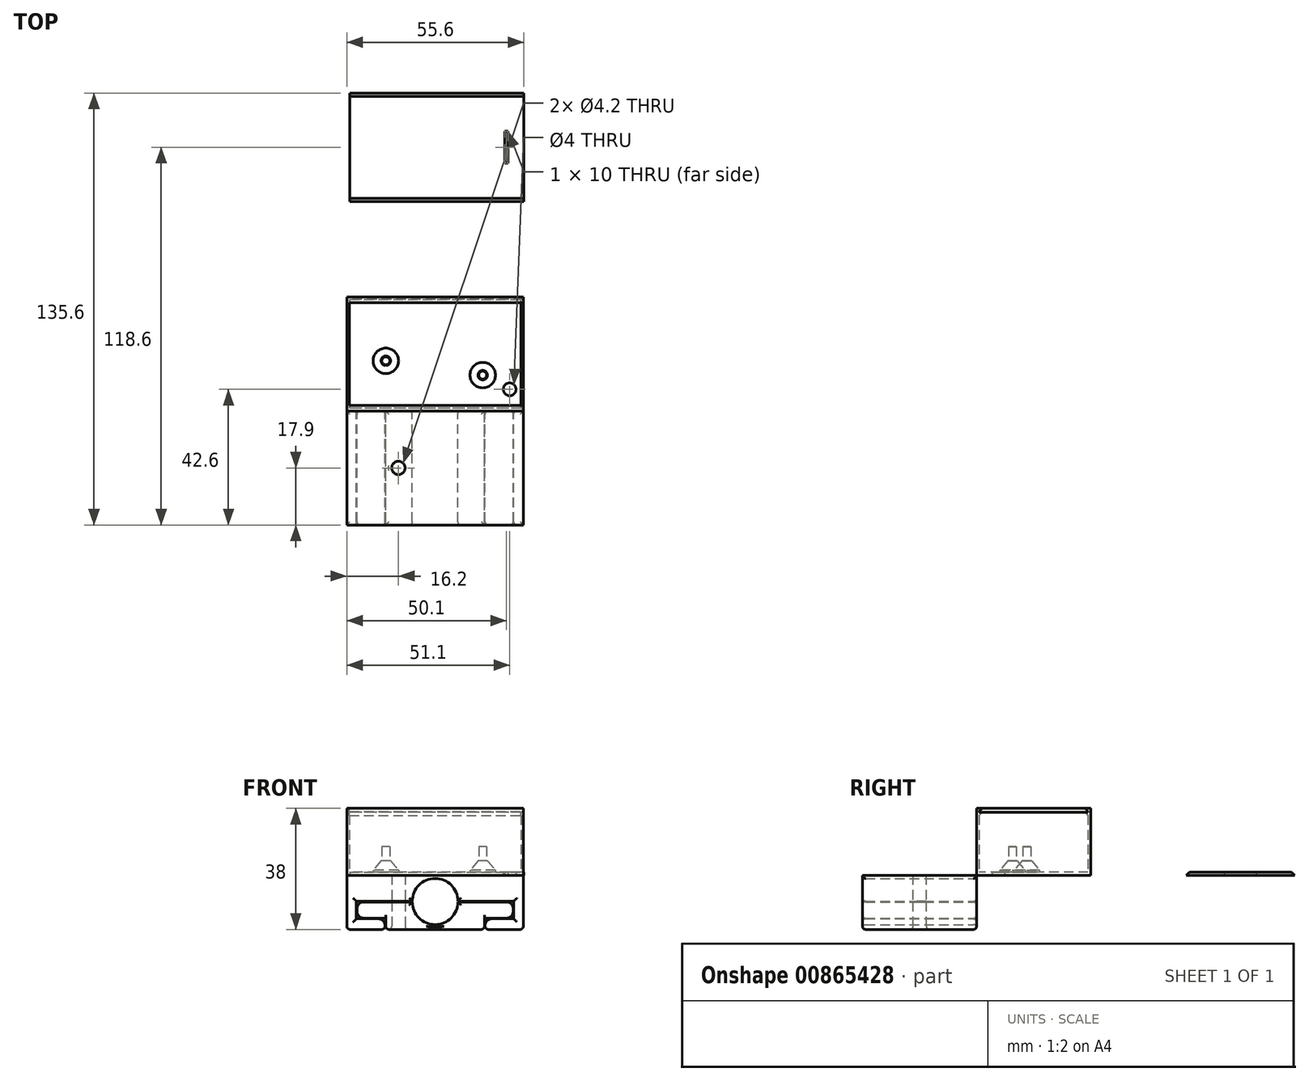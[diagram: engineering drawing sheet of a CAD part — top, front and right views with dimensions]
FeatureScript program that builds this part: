
annotation { "Feature Type Name" : "Feature", "Feature Type Description" : "" }
export const myFeature = defineFeature(function(context is Context, id is Id, definition is map)
    precondition{}
    {
        {
            var Q0;
            Q0=qCreatedBy(makeId("Top.planeOp"),FACE);
            var sketch = newSketch(context, id + "F0", { "sketchPlane" : qUnion([Q0])});
            skLineSegment(sketch, "E0.bottom", {"start": v(0, 0) * mm, "end": v(53.8, 0) * mm});
            skLineSegment(sketch, "E0.top", {"start": v(0, -34.2) * mm, "end": v(53.8, -34.2) * mm});
            skLineSegment(sketch, "E0.left", {"start": v(0, 0) * mm, "end": v(0, -34.2) * mm});
            skLineSegment(sketch, "E0.right", {"start": v(53.8, 0) * mm, "end": v(53.8, -34.2) * mm});
            skLineSegment(sketch, "E1.0", {"start": v(-0.8, 0.8) * mm, "end": v(54.6, 0.8) * mm});
            skLineSegment(sketch, "E1.1", {"start": v(-0.8, 0.8) * mm, "end": v(-0.8, -35) * mm});
            skLineSegment(sketch, "E1.2", {"start": v(-0.8, -35) * mm, "end": v(54.6, -35) * mm});
            skLineSegment(sketch, "E1.3", {"start": v(54.6, 0.8) * mm, "end": v(54.6, -35) * mm});
            skCircle(sketch, "E2", {"center": v(11.45, -19.25) * mm, "radius": 1.25 * mm});
            skCircle(sketch, "E3", {"center": v(11.45, -19.25) * mm, "radius": 4 * mm});
            skCircle(sketch, "E4", {"center": v(41.85, -23.75) * mm, "radius": 1.25 * mm});
            skCircle(sketch, "E5", {"center": v(41.85, -23.75) * mm, "radius": 4 * mm});
            skCircle(sketch, "E6", {"center": v(50.3, -28.2) * mm, "radius": 2 * mm});
            skLineSegment(sketch, "E7.bottom", {"start": v(54.8, 30.8) * mm, "end": v(0.2, 30.8) * mm});
            skLineSegment(sketch, "E7.top", {"start": v(54.8, 64.8) * mm, "end": v(0.2, 64.8) * mm});
            skLineSegment(sketch, "E7.left", {"start": v(54.8, 30.8) * mm, "end": v(54.8, 64.8) * mm});
            skLineSegment(sketch, "E7.right", {"start": v(0.2, 30.8) * mm, "end": v(0.2, 64.8) * mm});
            skLineSegment(sketch, "E8.bottom", {"start": v(48.8, 42.8) * mm, "end": v(49.8, 42.8) * mm});
            skLineSegment(sketch, "E8.top", {"start": v(48.8, 52.8) * mm, "end": v(49.8, 52.8) * mm});
            skLineSegment(sketch, "E8.left", {"start": v(48.8, 42.8) * mm, "end": v(48.8, 52.8) * mm});
            skLineSegment(sketch, "E8.right", {"start": v(49.8, 42.8) * mm, "end": v(49.8, 52.8) * mm});
            skLineSegment(sketch, "E9", {"start": v(54.8, 47.8) * mm, "end": v(0.2, 47.8) * mm, "construction": true});
            skLineSegment(sketch, "E10", {"start": v(49.8, 47.8) * mm, "end": v(48.8, 47.8) * mm, "construction": true});
            skSolve(sketch);
        }
        {
            var Q0;
            Q0=makeQuery(id+"F0.imprint","IMPRINT",FACE,{"disambiguationData":[TD([[makeQuery(id+"F0.imprint","IMPRINT",EDGE,{"derivedFrom":sQuery(id+"F0.wireOp",EDGE,"E0.bottom")}),1.0]])]});
            extrude(context, id + "F1", {"entities" : qUnion([Q0]), "depth" : 21 * mm, "offsetDistance" : 25 * mm});
        }
        {
            var Q0;
            Q0=makeQuery(id+"F0.imprint","IMPRINT",FACE,{"disambiguationData":[TD([[makeQuery(id+"F0.imprint","IMPRINT",EDGE,{"derivedFrom":sQuery(id+"F0.wireOp",EDGE,"E0.bottom")}),-1.0]])]});
            var Q1;
            Q1=makeQuery(id+"F0.imprint","IMPRINT",FACE,{"disambiguationData":[TD([[makeQuery(id+"F0.imprint","IMPRINT",EDGE,{"derivedFrom":sQuery(id+"F0.wireOp",EDGE,"E2")}),-1.0]])]});
            var Q2;
            Q2=makeQuery(id+"F0.imprint","IMPRINT",FACE,{"disambiguationData":[TD([[makeQuery(id+"F0.imprint","IMPRINT",EDGE,{"derivedFrom":sQuery(id+"F0.wireOp",EDGE,"E2")}),1.0]])]});
            var Q3;
            Q3=makeQuery(id+"F0.imprint","IMPRINT",FACE,{"disambiguationData":[TD([[makeQuery(id+"F0.imprint","IMPRINT",EDGE,{"derivedFrom":sQuery(id+"F0.wireOp",EDGE,"E4")}),-1.0]])]});
            var Q4;
            Q4=makeQuery(id+"F0.imprint","IMPRINT",FACE,{"disambiguationData":[TD([[makeQuery(id+"F0.imprint","IMPRINT",EDGE,{"derivedFrom":sQuery(id+"F0.wireOp",EDGE,"E4")}),1.0]])]});
            extrude(context, id + "F2", {"entities" : qUnion([Q0, Q1, Q2, Q3, Q4]), "operationType" : NewBodyOperationType.ADD, "depth" : 1 * mm, "offsetDistance" : 25 * mm});
        }
        {
            var Q0;
            Q0=makeQuery(id+"F0.imprint","IMPRINT",FACE,{"disambiguationData":[TD([[makeQuery(id+"F0.imprint","IMPRINT",EDGE,{"derivedFrom":sQuery(id+"F0.wireOp",EDGE,"E2")}),-1.0]])]});
            var Q1;
            Q1=makeQuery(id+"F0.imprint","IMPRINT",FACE,{"disambiguationData":[TD([[makeQuery(id+"F0.imprint","IMPRINT",EDGE,{"derivedFrom":sQuery(id+"F0.wireOp",EDGE,"E2")}),1.0]])]});
            var Q2;
            Q2=makeQuery(id+"F0.imprint","IMPRINT",FACE,{"disambiguationData":[TD([[makeQuery(id+"F0.imprint","IMPRINT",EDGE,{"derivedFrom":sQuery(id+"F0.wireOp",EDGE,"E4")}),1.0]])]});
            var Q3;
            Q3=makeQuery(id+"F0.imprint","IMPRINT",FACE,{"disambiguationData":[TD([[makeQuery(id+"F0.imprint","IMPRINT",EDGE,{"derivedFrom":sQuery(id+"F0.wireOp",EDGE,"E4")}),-1.0]])]});
            extrude(context, id + "F3", {"entities" : qUnion([Q0, Q1, Q2, Q3]), "operationType" : NewBodyOperationType.ADD, "depth" : 4.6 * mm, "offsetDistance" : 25 * mm});
        }
        {
            var Q0;
            Q0=makeQuery(id+"F0.imprint","IMPRINT",FACE,{"disambiguationData":[TD([[makeQuery(id+"F0.imprint","IMPRINT",EDGE,{"derivedFrom":sQuery(id+"F0.wireOp",EDGE,"E4")}),1.0]])]});
            var Q1;
            Q1=makeQuery(id+"F0.imprint","IMPRINT",FACE,{"disambiguationData":[TD([[makeQuery(id+"F0.imprint","IMPRINT",EDGE,{"derivedFrom":sQuery(id+"F0.wireOp",EDGE,"E2")}),1.0]])]});
            extrude(context, id + "F4", {"entities" : qUnion([Q0, Q1]), "operationType" : NewBodyOperationType.ADD, "depth" : 9 * mm, "offsetDistance" : 25 * mm});
        }
        {
            var Q0;
            Q0=makeQuery(id+"F3.opExtrude","CAP_EDGE",EDGE,{"disambiguationData":[OSD([sQuery(id+"F0.wireOp",EDGE,"E5")])],"isStart":false});
            var Q1;
            Q1=makeQuery(id+"F3.opExtrude","CAP_EDGE",EDGE,{"disambiguationData":[OSD([sQuery(id+"F0.wireOp",EDGE,"E3")])],"isStart":false});
            chamfer(context, id + "F5", {"entities" : qUnion([Q0, Q1]), "chamferType" : ChamferType.TWO_OFFSETS, "width1" : 2.5 * mm, "oppositeDirection" : false, "width2" : 3 * mm, "tangentPropagation" : true});
        }
        {
            var Q0;
            Q0=makeQuery(id+"F1.opExtrude","SWEPT_FACE",FACE,{"disambiguationData":[OSD([sQuery(id+"F0.wireOp",EDGE,"E0.top")])]});
            var sketch = newSketch(context, id + "F6", { "sketchPlane" : qUnion([Q0])});
            skLineSegment(sketch, "E11", {"start": v(-53.8, 20) * mm, "end": v(0, 20) * mm});
            skLineSegment(sketch, "E12", {"start": v(-53.8, 19.8) * mm, "end": v(0, 19.8) * mm});
            skLineSegment(sketch, "E13", {"start": v(-53.8, 18.8) * mm, "end": v(0, 18.8) * mm});
            skSolve(sketch);
        }
        {
            var Q0;
            Q0=makeQuery(id+"F1.opExtrude","SWEPT_FACE",FACE,{"disambiguationData":[OSD([sQuery(id+"F0.wireOp",EDGE,"E0.bottom")])]});
            var sketch = newSketch(context, id + "F7", { "sketchPlane" : qUnion([Q0])});
            skLineSegment(sketch, "E14", {"start": v(0, 20) * mm, "end": v(53.8, 20) * mm});
            skLineSegment(sketch, "E15", {"start": v(53.8, 19.8) * mm, "end": v(0, 19.8) * mm});
            skLineSegment(sketch, "E16", {"start": v(0, 18.8) * mm, "end": v(53.8, 18.8) * mm});
            skSolve(sketch);
        }
        {
            var Q0;
            {var subQ0=sQuery(id+"F6.wireOp",EDGE,"E11");Q0=makeQuery(id+"F6.imprint","IMPRINT",FACE,{"disambiguationData":[TD([[makeQuery(id+"F6.imprint","IMPRINT",EDGE,{"derivedFrom":subQ0}),1.0]])]});}
            var Q1;
            {var subQ0=sQuery(id+"F6.wireOp",EDGE,"E12");Q1=makeQuery(id+"F6.imprint","IMPRINT",FACE,{"disambiguationData":[TD([[makeQuery(id+"F6.imprint","IMPRINT",EDGE,{"derivedFrom":subQ0}),-1.0]])]});}
            extrude(context, id + "F8", {"entities" : qUnion([Q0, Q1]), "operationType" : NewBodyOperationType.ADD, "depth" : 1 * mm, "offsetDistance" : 25 * mm});
        }
        {
            var Q0;
            {var subQ0=sQuery(id+"F7.wireOp",EDGE,"E15");Q0=makeQuery(id+"F7.imprint","IMPRINT",FACE,{"disambiguationData":[TD([[makeQuery(id+"F7.imprint","IMPRINT",EDGE,{"derivedFrom":subQ0}),1.0]])]});}
            var Q1;
            {var subQ0=sQuery(id+"F7.wireOp",EDGE,"E14");Q1=makeQuery(id+"F7.imprint","IMPRINT",FACE,{"disambiguationData":[TD([[makeQuery(id+"F7.imprint","IMPRINT",EDGE,{"derivedFrom":subQ0}),1.0]])]});}
            extrude(context, id + "F9", {"entities" : qUnion([Q0, Q1]), "operationType" : NewBodyOperationType.ADD, "depth" : 1 * mm, "offsetDistance" : 25 * mm});
        }
        {
            var Q0;
            Q0=makeQuery(id+"F9.opExtrude","CAP_EDGE",EDGE,{"disambiguationData":[OSD([sQuery(id+"F7.wireOp",EDGE,"E16")])],"isStart":false});
            var Q1;
            Q1=makeQuery(id+"F9.opExtrude","CAP_EDGE",EDGE,{"disambiguationData":[OSD([sQuery(id+"F7.wireOp",EDGE,"E14")])],"isStart":false});
            var Q2;
            Q2=makeQuery(id+"F8.opExtrude","CAP_EDGE",EDGE,{"disambiguationData":[OSD([sQuery(id+"F6.wireOp",EDGE,"E13")])],"isStart":false});
            var Q3;
            Q3=makeQuery(id+"F8.opExtrude","CAP_EDGE",EDGE,{"disambiguationData":[OSD([sQuery(id+"F6.wireOp",EDGE,"E11")])],"isStart":false});
            chamfer(context, id + "F10", {"entities" : qUnion([Q0, Q1, Q2, Q3]), "width" : 1 * mm, "tangentPropagation" : true});
        }
        {
            var Q0;
            Q0=makeQuery(id+"F1.opExtrude","SWEPT_FACE",FACE,{"disambiguationData":[OSD([sQuery(id+"F0.wireOp",EDGE,"E0.right")])]});
            var sketch = newSketch(context, id + "F11", { "sketchPlane" : qUnion([Q0])});
            skLineSegment(sketch, "E17", {"start": v(1, 19.8) * mm, "end": v(33.2, 19.8) * mm});
            skSolve(sketch);
        }
        {
            var Q0;
            Q0=makeQuery(id+"F11.imprint","IMPRINT",FACE,{"disambiguationData":[TD([[makeQuery(id+"F11.imprint","IMPRINT",EDGE,{"derivedFrom":sQuery(id+"F11.wireOp",EDGE,"E17")}),1.0]])]});
            extrude(context, id + "F12", {"entities" : qUnion([Q0]), "operationType" : NewBodyOperationType.REMOVE, "endBound" : BoundingType.UP_TO_NEXT, "oppositeDirection" : true, "depth" : 25 * mm, "offsetDistance" : 25 * mm});
        }
        {
            var Q0;
            Q0=makeQuery(id+"F0.imprint","IMPRINT",FACE,{"disambiguationData":[TD([[makeQuery(id+"F0.imprint","IMPRINT",EDGE,{"derivedFrom":sQuery(id+"F0.wireOp",EDGE,"E7.bottom")}),-1.0]])]});
            extrude(context, id + "F13", {"entities" : qUnion([Q0]), "depth" : 1 * mm, "offsetDistance" : 25 * mm});
        }
        {
            var Q0;
            Q0=makeQuery(id+"F13.opExtrude","CAP_EDGE",EDGE,{"disambiguationData":[OSD([sQuery(id+"F0.wireOp",EDGE,"E7.bottom")])],"isStart":false});
            var Q1;
            Q1=makeQuery(id+"F13.opExtrude","CAP_EDGE",EDGE,{"disambiguationData":[OSD([sQuery(id+"F0.wireOp",EDGE,"E7.top")])],"isStart":false});
            chamfer(context, id + "F14", {"entities" : qUnion([Q0, Q1]), "width" : 1 * mm, "tangentPropagation" : true});
        }
        {
            var Q0;
            Q0=makeQuery(id+"F1.opExtrude","SWEPT_FACE",FACE,{"disambiguationData":[OSD([sQuery(id+"F0.wireOp",EDGE,"E1.2")])]});
            var sketch = newSketch(context, id + "F15", { "sketchPlane" : qUnion([Q0])});
            skLineSegment(sketch, "E18", {"start": v(26.9, -1) * mm, "end": v(26.9, -8.15) * mm, "construction": true});
            skArc(sketch, "E19", {"start": v(34.05, -8.15) * mm, "mid": v(26.9, -1) * mm, "end": v(19.75, -8.15) * mm});
            skLineSegment(sketch, "E20", {"start": v(54.6, 0) * mm, "end": v(54.6, -8.15) * mm});
            skLineSegment(sketch, "E21", {"start": v(-0.8, 0) * mm, "end": v(54.6, 0) * mm});
            skLineSegment(sketch, "E22", {"start": v(26.9, 0) * mm, "end": v(26.9, -1) * mm, "construction": true});
            skLineSegment(sketch, "E23", {"start": v(51.6, -8.15) * mm, "end": v(34.05, -8.15) * mm});
            skLineSegment(sketch, "E24", {"start": v(19.75, -8.15) * mm, "end": v(2.2, -8.15) * mm});
            skLineSegment(sketch, "E25", {"start": v(26.9, -8.15) * mm, "end": v(26.9, -15.5) * mm, "construction": true});
            skArc(sketch, "E26", {"start": v(19.75, -8.35) * mm, "mid": v(21.84, -13.4) * mm, "end": v(26.9, -15.5) * mm});
            skLineSegment(sketch, "E27", {"start": v(26.9, -17) * mm, "end": v(11.4, -17) * mm});
            skLineSegment(sketch, "E28", {"start": v(-0.8, 0) * mm, "end": v(-0.8, -17) * mm});
            skLineSegment(sketch, "E29", {"start": v(-0.8, -17) * mm, "end": v(11.2, -17) * mm});
            skLineSegment(sketch, "E30", {"start": v(11.2, -17) * mm, "end": v(11.2, -13.68) * mm});
            skLineSegment(sketch, "E31", {"start": v(11.2, -13.68) * mm, "end": v(2.2, -13.68) * mm});
            skLineSegment(sketch, "E32", {"start": v(2.2, -13.68) * mm, "end": v(2.2, -8.15) * mm});
            skLineSegment(sketch, "E33.1", {"start": v(19.75, -8.35) * mm, "end": v(2.4, -8.35) * mm});
            skLineSegment(sketch, "E33.2", {"start": v(2.4, -13.48) * mm, "end": v(2.4, -8.35) * mm});
            skLineSegment(sketch, "E33.3", {"start": v(11.4, -13.48) * mm, "end": v(2.4, -13.48) * mm});
            skLineSegment(sketch, "E34.MirrorCS", {"start": v(26.9, -17) * mm, "end": v(42.4, -17) * mm});
            skLineSegment(sketch, "E35.MirrorCS", {"start": v(42.4, -13.48) * mm, "end": v(51.4, -13.48) * mm});
            skLineSegment(sketch, "E36.MirrorCS", {"start": v(51.4, -13.48) * mm, "end": v(51.4, -8.35) * mm});
            skLineSegment(sketch, "E37.MirrorCS", {"start": v(34.05, -8.35) * mm, "end": v(51.4, -8.35) * mm});
            skArc(sketch, "E38.MirrorCS", {"start": v(34.05, -8.35) * mm, "mid": v(31.96, -13.4) * mm, "end": v(26.9, -15.5) * mm});
            skLineSegment(sketch, "E39.MirrorCS", {"start": v(42.6, -17) * mm, "end": v(42.6, -13.68) * mm});
            skLineSegment(sketch, "E40.MirrorCS", {"start": v(54.6, -17) * mm, "end": v(42.6, -17) * mm});
            skLineSegment(sketch, "E41.MirrorCS", {"start": v(42.6, -13.68) * mm, "end": v(51.6, -13.68) * mm});
            skLineSegment(sketch, "E42.MirrorCS", {"start": v(51.6, -13.68) * mm, "end": v(51.6, -8.15) * mm});
            skLineSegment(sketch, "E43.MirrorCS", {"start": v(54.6, 0) * mm, "end": v(54.6, -17) * mm});
            skLineSegment(sketch, "E44", {"start": v(11.4, -13.48) * mm, "end": v(11.4, -17) * mm});
            skLineSegment(sketch, "E45.MirrorCS", {"start": v(42.4, -13.48) * mm, "end": v(42.4, -17) * mm});
            skSolve(sketch);
        }
        {
            var Q0;
            Q0=makeQuery(id+"F15.imprint","IMPRINT",FACE,{"disambiguationData":[TD([[makeQuery(id+"F15.imprint","IMPRINT",EDGE,{"derivedFrom":sQuery(id+"F15.wireOp",EDGE,"E19")}),-1.0]])]});
            var Q1;
            Q1=makeQuery(id+"F15.imprint","IMPRINT",FACE,{"disambiguationData":[TD([[makeQuery(id+"F15.imprint","IMPRINT",EDGE,{"derivedFrom":sQuery(id+"F15.wireOp",EDGE,"E26")}),-1.0]])]});
            extrude(context, id + "F16", {"entities" : qUnion([Q0, Q1]), "depth" : 35.8 * mm, "offsetDistance" : 25 * mm});
        }
        {
            var Q0;
            Q0=makeQuery(id+"F16.opExtrude","SWEPT_FACE",FACE,{"disambiguationData":[OSD([sQuery(id+"F15.wireOp",EDGE,"E27")])]});
            var sketch = newSketch(context, id + "F17", { "sketchPlane" : qUnion([Q0])});
            skLineSegment(sketch, "E46", {"start": v(50.6, 52.9) * mm, "end": v(11.4, 52.9) * mm, "construction": true});
            skCircle(sketch, "E47", {"center": v(15.4, 52.9) * mm, "radius": 2.1 * mm});
            skCircle(sketch, "E48", {"center": v(15.4, 52.9) * mm, "radius": 3.2 * mm});
            skSolve(sketch);
        }
        {
            var Q0;
            Q0=makeQuery(id+"F17.imprint","IMPRINT",FACE,{"disambiguationData":[TD([[makeQuery(id+"F17.imprint","IMPRINT",EDGE,{"derivedFrom":sQuery(id+"F17.wireOp",EDGE,"E47")}),1.0]])]});
            extrude(context, id + "F18", {"entities" : qUnion([Q0]), "operationType" : NewBodyOperationType.REMOVE, "oppositeDirection" : true, "depth" : 25 * mm, "offsetDistance" : 25 * mm});
        }
        {
            var Q0;
            Q0=makeQuery(id+"F16.opExtrude","SWEPT_EDGE",EDGE,{"disambiguationData":[OSD([sQuery(id+"F15.wireOp",EDGE,"E33.1"),sQuery(id+"F15.wireOp",EDGE,"E33.2")])]});
            var Q1;
            Q1=makeQuery(id+"F16.opExtrude","SWEPT_EDGE",EDGE,{"disambiguationData":[OSD([sQuery(id+"F15.wireOp",EDGE,"E30"),sQuery(id+"F15.wireOp",EDGE,"E31")])]});
            var Q2;
            Q2=makeQuery(id+"F16.opExtrude","SWEPT_EDGE",EDGE,{"disambiguationData":[OSD([sQuery(id+"F15.wireOp",EDGE,"E33.2"),sQuery(id+"F15.wireOp",EDGE,"E33.3")])]});
            var Q3;
            Q3=makeQuery(id+"F16.opExtrude","SWEPT_EDGE",EDGE,{"disambiguationData":[OSD([sQuery(id+"F15.wireOp",EDGE,"E35.MirrorCS"),sQuery(id+"F15.wireOp",EDGE,"E36.MirrorCS")])]});
            var Q4;
            Q4=makeQuery(id+"F16.opExtrude","SWEPT_EDGE",EDGE,{"disambiguationData":[OSD([sQuery(id+"F15.wireOp",EDGE,"E36.MirrorCS"),sQuery(id+"F15.wireOp",EDGE,"E37.MirrorCS")])]});
            var Q5;
            Q5=makeQuery(id+"F16.opExtrude","SWEPT_EDGE",EDGE,{"disambiguationData":[OSD([sQuery(id+"F15.wireOp",EDGE,"E39.MirrorCS"),sQuery(id+"F15.wireOp",EDGE,"E41.MirrorCS")])]});
            fillet(context, id + "F19", {"entities" : qUnion([Q0, Q1, Q2, Q3, Q4, Q5]), "radius" : 2.1 * mm, "tangentPropagation" : true, "allowEdgeOverflow" : false});
        }
        {
            var Q0;
            Q0=makeQuery(id+"F16.opExtrude","CAP_EDGE",EDGE,{"disambiguationData":[OSD([sQuery(id+"F15.wireOp",EDGE,"E33.1")])],"isStart":true});
            var Q1;
            Q1=makeQuery(id+"F16.opExtrude","CAP_EDGE",EDGE,{"disambiguationData":[OSD([sQuery(id+"F15.wireOp",EDGE,"E33.0")])],"isStart":true});
            var Q2;
            Q2=makeQuery(id+"F16.opExtrude","CAP_EDGE",EDGE,{"disambiguationData":[OSD([sQuery(id+"F15.wireOp",EDGE,"814235ba-19f5-4b85-ac29-dc1e294b29660.MirrorCS")])],"isStart":true});
            var Q3;
            Q3=makeQuery(id+"F16.opExtrude","CAP_EDGE",EDGE,{"disambiguationData":[OSD([sQuery(id+"F15.wireOp",EDGE,"E35.MirrorCS")])],"isStart":true});
            var Q4;
            Q4=makeQuery(id+"F16.opExtrude","CAP_EDGE",EDGE,{"disambiguationData":[OSD([sQuery(id+"F15.wireOp",EDGE,"814235ba-19f5-4b85-ac29-dc1e294b29660.MirrorCS")])],"isStart":false});
            var Q5;
            Q5=makeQuery(id+"F16.opExtrude","CAP_EDGE",EDGE,{"disambiguationData":[OSD([sQuery(id+"F15.wireOp",EDGE,"E35.MirrorCS")])],"isStart":false});
            var Q6;
            Q6=makeQuery(id+"F16.opExtrude","CAP_EDGE",EDGE,{"disambiguationData":[OSD([sQuery(id+"F15.wireOp",EDGE,"E33.1")])],"isStart":false});
            var Q7;
            Q7=makeQuery(id+"F16.opExtrude","CAP_EDGE",EDGE,{"disambiguationData":[OSD([sQuery(id+"F15.wireOp",EDGE,"E33.0")])],"isStart":false});
            var Q8;
            Q8=makeQuery(id+"F16.opExtrude","CAP_EDGE",EDGE,{"disambiguationData":[OSD([sQuery(id+"F15.wireOp",EDGE,"E19")])],"isStart":false});
            var Q9;
            Q9=makeQuery(id+"F16.opExtrude","CAP_EDGE",EDGE,{"disambiguationData":[OSD([sQuery(id+"F15.wireOp",EDGE,"E26"),sQuery(id+"F15.wireOp",EDGE,"E38.MirrorCS")])],"isStart":false});
            var Q10;
            Q10=makeQuery(id+"F16.opExtrude","CAP_EDGE",EDGE,{"disambiguationData":[OSD([sQuery(id+"F15.wireOp",EDGE,"E26"),sQuery(id+"F15.wireOp",EDGE,"E38.MirrorCS")])],"isStart":true});
            var Q11;
            Q11=makeQuery(id+"F16.opExtrude","CAP_EDGE",EDGE,{"disambiguationData":[OSD([sQuery(id+"F15.wireOp",EDGE,"E19")])],"isStart":true});
            var Q12;
            Q12=makeQuery(id+"F16.opExtrude","CAP_EDGE",EDGE,{"disambiguationData":[OSD([sQuery(id+"F15.wireOp",EDGE,"E23")])],"isStart":true});
            var Q13;
            Q13=makeQuery(id+"F16.opExtrude","CAP_EDGE",EDGE,{"disambiguationData":[OSD([sQuery(id+"F15.wireOp",EDGE,"E42.MirrorCS")])],"isStart":true});
            var Q14;
            Q14=makeQuery(id+"F16.opExtrude","CAP_EDGE",EDGE,{"disambiguationData":[OSD([sQuery(id+"F15.wireOp",EDGE,"E41.MirrorCS")])],"isStart":true});
            var Q15;
            Q15=makeQuery(id+"F16.opExtrude","CAP_EDGE",EDGE,{"disambiguationData":[OSD([sQuery(id+"F15.wireOp",EDGE,"E31")])],"isStart":true});
            var Q16;
            Q16=makeQuery(id+"F16.opExtrude","CAP_EDGE",EDGE,{"disambiguationData":[OSD([sQuery(id+"F15.wireOp",EDGE,"E32")])],"isStart":true});
            var Q17;
            Q17=makeQuery(id+"F16.opExtrude","CAP_EDGE",EDGE,{"disambiguationData":[OSD([sQuery(id+"F15.wireOp",EDGE,"E24")])],"isStart":true});
            var Q18;
            Q18=makeQuery(id+"F16.opExtrude","CAP_EDGE",EDGE,{"disambiguationData":[OSD([sQuery(id+"F15.wireOp",EDGE,"E41.MirrorCS")])],"isStart":false});
            var Q19;
            Q19=makeQuery(id+"F16.opExtrude","CAP_EDGE",EDGE,{"disambiguationData":[OSD([sQuery(id+"F15.wireOp",EDGE,"E40.MirrorCS")])],"isStart":false});
            var Q20;
            Q20=makeQuery(id+"F16.opExtrude","SWEPT_EDGE",EDGE,{"disambiguationData":[OSD([sQuery(id+"F15.wireOp",EDGE,"E40.MirrorCS"),sQuery(id+"F15.wireOp",EDGE,"E43.MirrorCS")])]});
            var Q21;
            Q21=makeQuery(id+"F16.opExtrude","CAP_EDGE",EDGE,{"disambiguationData":[OSD([sQuery(id+"F15.wireOp",EDGE,"E40.MirrorCS")])],"isStart":true});
            var Q22;
            Q22=makeQuery(id+"F16.opExtrude","CAP_EDGE",EDGE,{"disambiguationData":[OSD([sQuery(id+"F15.wireOp",EDGE,"E29")])],"isStart":false});
            var Q23;
            Q23=makeQuery(id+"F16.opExtrude","SWEPT_FACE",FACE,{"disambiguationData":[OSD([sQuery(id+"F15.wireOp",EDGE,"E29")])]});
            var Q24;
            Q24=makeQuery(id+"F16.opExtrude","SWEPT_FACE",FACE,{"disambiguationData":[OSD([sQuery(id+"F15.wireOp",EDGE,"E40.MirrorCS")])]});
            var Q25;
            Q25=makeQuery(id+"F16.opExtrude","SWEPT_FACE",FACE,{"disambiguationData":[OSD([sQuery(id+"F15.wireOp",EDGE,"E27"),sQuery(id+"F15.wireOp",EDGE,"E34.MirrorCS")])]});
            var Q26;
            Q26=makeQuery(id+"F16.opExtrude","CAP_EDGE",EDGE,{"disambiguationData":[OSD([sQuery(id+"F15.wireOp",EDGE,"E32")])],"isStart":false});
            var Q27;
            Q27=makeQuery(id+"F16.opExtrude","CAP_EDGE",EDGE,{"disambiguationData":[OSD([sQuery(id+"F15.wireOp",EDGE,"E31")])],"isStart":false});
            var Q28;
            Q28=makeQuery(id+"F16.opExtrude","CAP_EDGE",EDGE,{"disambiguationData":[OSD([sQuery(id+"F15.wireOp",EDGE,"E42.MirrorCS")])],"isStart":false});
            var Q29;
            Q29=makeQuery(id+"F16.opExtrude","CAP_EDGE",EDGE,{"disambiguationData":[OSD([sQuery(id+"F15.wireOp",EDGE,"E24")])],"isStart":false});
            var Q30;
            Q30=makeQuery(id+"F16.opExtrude","CAP_EDGE",EDGE,{"disambiguationData":[OSD([sQuery(id+"F15.wireOp",EDGE,"E23")])],"isStart":false});
            fillet(context, id + "F20", {"entities" : qUnion([Q0, Q1, Q2, Q3, Q4, Q5, Q6, Q7, Q8, Q9, Q10, Q11, Q12, Q13, Q14, Q15, Q16, Q17, Q18, Q19, Q20, Q21, Q22, Q23, Q24, Q25, Q26, Q27, Q28, Q29, Q30]), "radius" : 1 * mm, "tangentPropagation" : true, "allowEdgeOverflow" : false});
        }
    });
